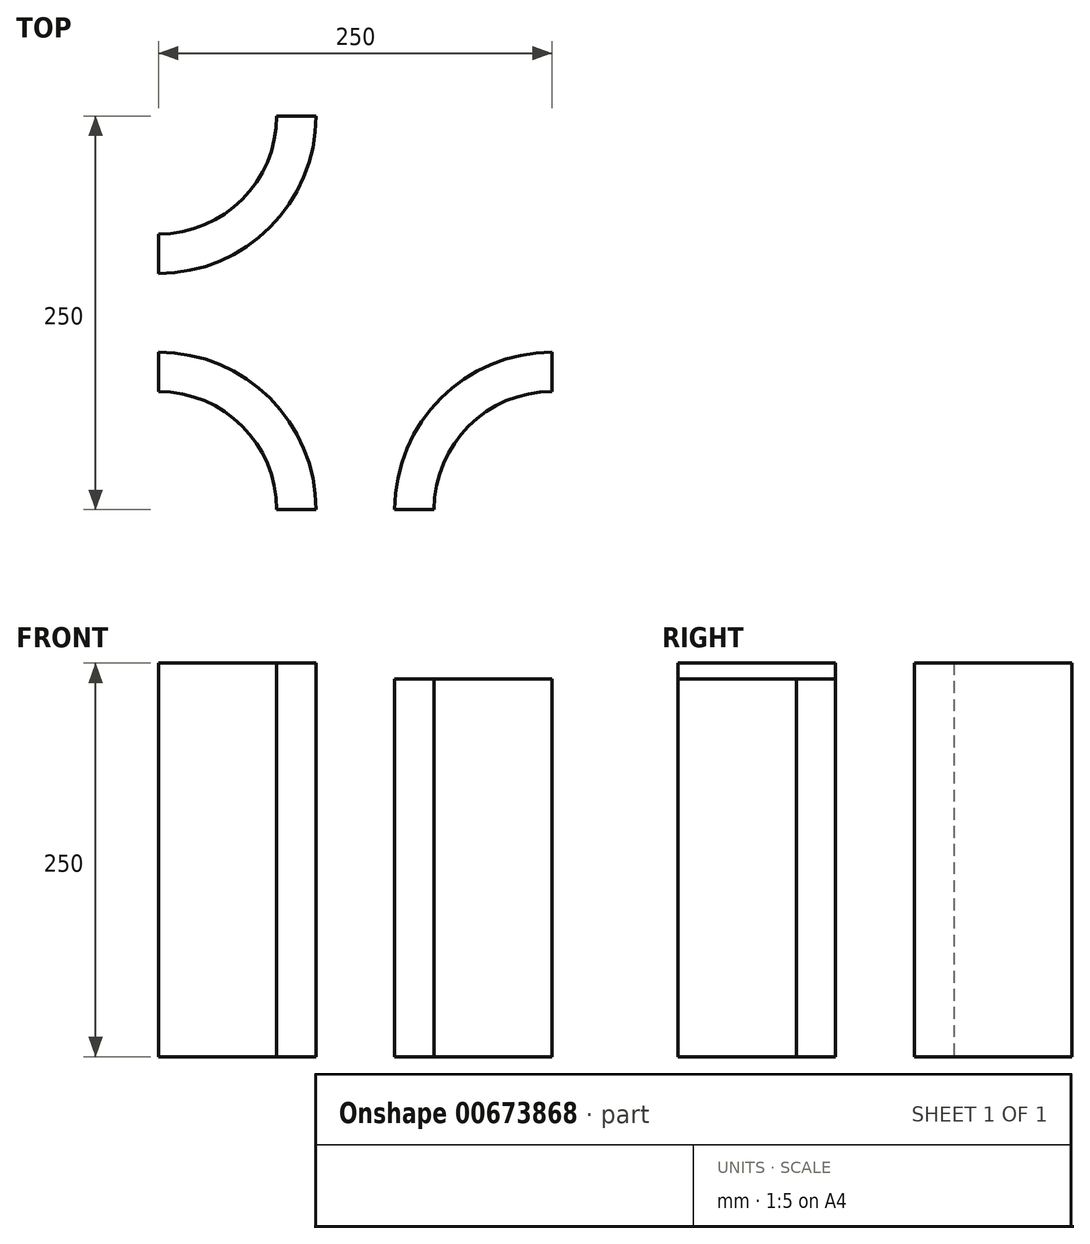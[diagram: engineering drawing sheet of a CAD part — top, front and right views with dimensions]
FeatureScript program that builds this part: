
annotation { "Feature Type Name" : "Feature", "Feature Type Description" : "" }
export const myFeature = defineFeature(function(context is Context, id is Id, definition is map)
    precondition{}
    {
        {
            var Q0;
            Q0=qCreatedBy(makeId("Top.planeOp"),FACE);
            var sketch = newSketch(context, id + "F0", { "sketchPlane" : qUnion([Q0])});
            skLineSegment(sketch, "E0", {"start": v(-250, 75) * mm, "end": v(-250, 175) * mm});
            skLineSegment(sketch, "E1", {"start": v(-175, 250) * mm, "end": v(-75, 250) * mm});
            skLineSegment(sketch, "E2", {"start": v(0, 100) * mm, "end": v(0, 175) * mm});
            skLineSegment(sketch, "E3", {"start": v(-100, 0) * mm, "end": v(-175, 0) * mm});
            skLineSegment(sketch, "E4", {"start": v(0, 100) * mm, "end": v(0, 75) * mm});
            skLineSegment(sketch, "E5", {"start": v(-100, 0) * mm, "end": v(-75, 0) * mm});
            skArc(sketch, "E6", {"start": v(-250, 175) * mm, "mid": v(-196.97, 196.97) * mm, "end": v(-175, 250) * mm});
            skLineSegment(sketch, "E7", {"start": v(-175, 250) * mm, "end": v(-150, 250) * mm});
            skLineSegment(sketch, "E8", {"start": v(-250, 175) * mm, "end": v(-250, 150) * mm});
            skArc(sketch, "E9", {"start": v(-250, 150) * mm, "mid": v(-179.29, 179.29) * mm, "end": v(-150, 250) * mm});
            skLineSegment(sketch, "E10", {"start": v(0, 175) * mm, "end": v(0, 150) * mm});
            skLineSegment(sketch, "E11", {"start": v(-75, 250) * mm, "end": v(-100, 250) * mm});
            skArc(sketch, "E12", {"start": v(-75, 250) * mm, "mid": v(-53.03, 196.97) * mm, "end": v(0, 175) * mm});
            skArc(sketch, "E13", {"start": v(-100, 250) * mm, "mid": v(-70.71, 179.29) * mm, "end": v(0, 150) * mm});
            skLineSegment(sketch, "E14", {"start": v(-250, 75) * mm, "end": v(-250, 100) * mm});
            skLineSegment(sketch, "E15", {"start": v(-175, 0) * mm, "end": v(-150, 0) * mm});
            skArc(sketch, "E16", {"start": v(-175, 0) * mm, "mid": v(-196.97, 53.03) * mm, "end": v(-250, 75) * mm});
            skArc(sketch, "E17", {"start": v(-150, 0) * mm, "mid": v(-179.29, 70.71) * mm, "end": v(-250, 100) * mm});
            skArc(sketch, "E18.trimOffspring", {"start": v(0, 75) * mm, "mid": v(-53.03, 53.03) * mm, "end": v(-75, 0) * mm});
            skArc(sketch, "E19.trimOffspring", {"start": v(0, 100) * mm, "mid": v(-70.71, 70.71) * mm, "end": v(-100, 0) * mm});
            skPoint(sketch, "E20.end.orphan", {"position": v(0, -250) * mm});
            skPoint(sketch, "E21.orphan", {"position": v(250, 250) * mm});
            skPoint(sketch, "E22.start.orphan", {"position": v(250, 0) * mm});
            skPoint(sketch, "E23.orphan", {"position": v(250, -250) * mm});
            skPoint(sketch, "E24.end.orphan", {"position": v(-250, -250) * mm});
            skSolve(sketch);
        }
        {
            var Q0;
            Q0=makeQuery(id+"F0.imprint","IMPRINT",FACE,{"disambiguationData":[TD([[makeQuery(id+"F0.imprint","IMPRINT",EDGE,{"derivedFrom":sQuery(id+"F0.wireOp",EDGE,"E0")}),-1.0]])]});
            extrude(context, id + "F1", {"entities" : qUnion([Q0]), "depth" : 250 * mm, "offsetDistance" : 25 * mm});
        }
        {
            var Q0;
            Q0=makeQuery(id+"F0.imprint","IMPRINT",FACE,{"disambiguationData":[TD([[makeQuery(id+"F0.imprint","IMPRINT",EDGE,{"derivedFrom":sQuery(id+"F0.wireOp",EDGE,"E6")}),-1.0]])]});
            var Q1;
            Q1=makeQuery(id+"F0.imprint","IMPRINT",FACE,{"disambiguationData":[TD([[makeQuery(id+"F0.imprint","IMPRINT",EDGE,{"derivedFrom":sQuery(id+"F0.wireOp",EDGE,"E14")}),-1.0]])]});
            var Q2;
            Q2=makeQuery(id+"F0.imprint","IMPRINT",FACE,{"disambiguationData":[TD([[makeQuery(id+"F0.imprint","IMPRINT",EDGE,{"derivedFrom":sQuery(id+"F0.wireOp",EDGE,"E4")}),-1.0]])]});
            var Q3;
            Q3=makeQuery(id+"F0.imprint","IMPRINT",FACE,{"disambiguationData":[TD([[makeQuery(id+"F0.imprint","IMPRINT",EDGE,{"derivedFrom":sQuery(id+"F0.wireOp",EDGE,"E10")}),-1.0]])]});
            extrude(context, id + "F2", {"entities" : qUnion([Q0, Q1, Q2, Q3]), "operationType" : NewBodyOperationType.ADD, "depth" : 240 * mm, "offsetDistance" : 25 * mm});
        }
    });
